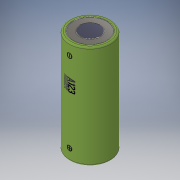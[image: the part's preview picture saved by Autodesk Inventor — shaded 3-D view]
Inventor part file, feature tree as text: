
AUTODESK INVENTOR PART (.ipt)
format: ipt  version: 2019.2 (Build 232265000, 265)  size: 1,036,800 bytes
history: native  units: mm
features: sketch x4, fillet x2, emboss x2, revolve x1, extrude x1, plane x1
ambient origin geometry x8: Origin, YZ Plane, XZ Plane, XY Plane, X Axis, Y Axis, Z Axis, Center Point
bodies: Solid1 (feature_tree)
feature tree (11):
  revolve  "Revolution1"  [1 undecoded]
  fillet  "Fillet1"  [1 undecoded]
  extrude  "Extrusion1"  Depth=13.0mm
  fillet  "Fillet2"  Radius=21.0mm
  plane  "Work Plane1"
  emboss  "Emboss1"
  emboss  "Emboss2"
  sketch  "Sketch1"  dims[d0=65.0mm d1=13.0mm d2=90.0deg]
  sketch  "Sketch2"  dims[d3=1.0mm d4=13.0mm d5=21.0mm]
  sketch  "Sketch3"  dims[d6=0.2mm d7=0.0mm]
  sketch  "Sketch4"  dims[d8=0.5mm d9=2.0mm d10=2.0mm d11=2.0mm d12=2.0mm d13=2.0mm d14=2.0mm d15=0.01mm d16=0.174533mm d18=0.1mm d19=8.0mm d20=9.0mm d21=0.01mm d22=0.174533mm d23=3.5mm]
note: 2 required parameter values undecoded (feature->parameter linkage not recoverable at this tier; creation-order binding heuristic only, values carry confidence <= 0.55)